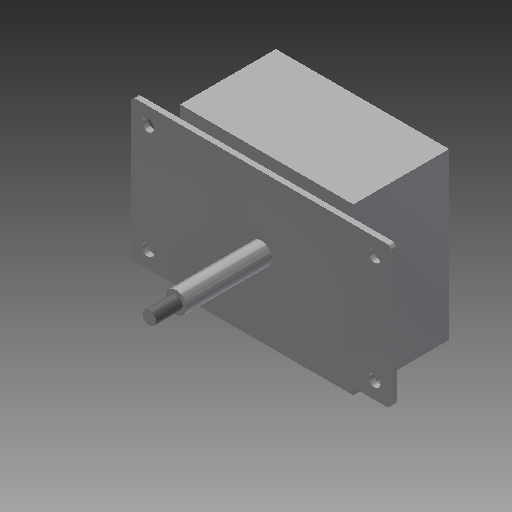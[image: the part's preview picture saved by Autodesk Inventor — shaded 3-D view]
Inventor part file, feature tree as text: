
AUTODESK INVENTOR PART (.ipt)
format: ipt  version: 2019 (Build 230136000, 136)  size: 154,624 bytes
history: native  units: mm
features: extrude x4, other x4, fillet x1, hole x1, thread x1
ambient origin geometry x8: Origin, YZ Plane, XZ Plane, XY Plane, X Axis, Y Axis, Z Axis, Center Point
bodies: Solid1 (feature_tree), BodySketch (feature_tree)
feature tree (11):
  extrude  "JoystickMountPlate"  Depth=53.0mm
  fillet  "MountPlateCornerFillet"  Radius=98.0mm
  extrude  "JoystickBody"  Depth=2.0mm TaperAngle=0.0deg
  extrude  "Shaft"  Depth=2.0mm
  extrude  "ShaftScrew"  Depth=65.0mm
  other  "ShaftThread"
  hole  "MountingHoles"  [1 undecoded]
  other  "JoystickMount"
  other  "JoystickPostCenter"
  thread  "ThreadSketch"  [1 undecoded]
  other  "MountHoles"
note: 2 required parameter values undecoded (feature->parameter linkage not recoverable at this tier; creation-order binding heuristic only, values carry confidence <= 0.55)
